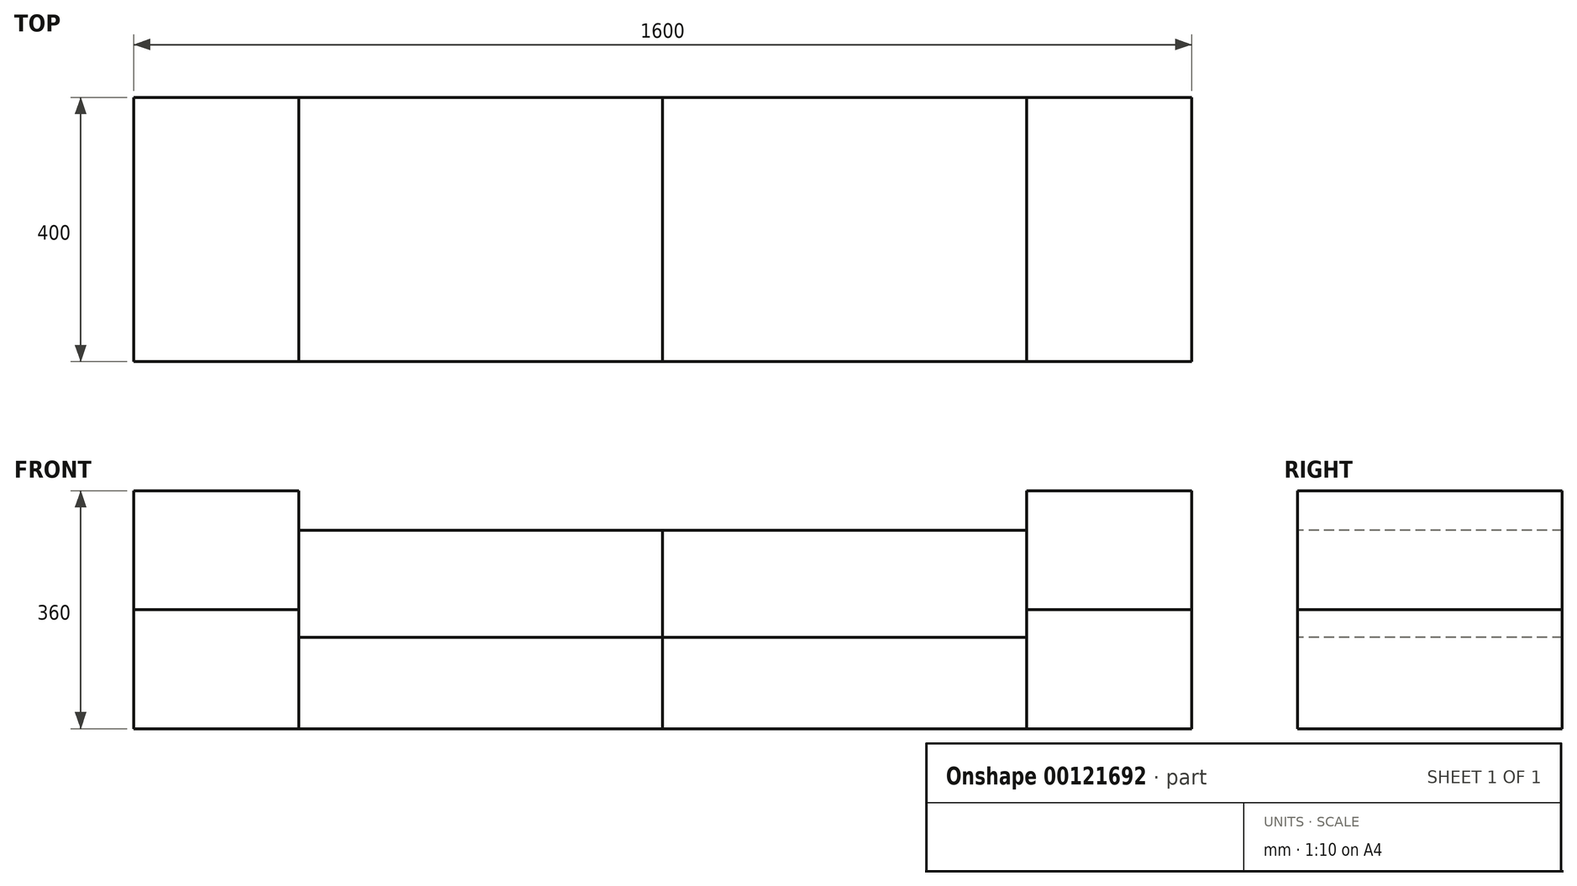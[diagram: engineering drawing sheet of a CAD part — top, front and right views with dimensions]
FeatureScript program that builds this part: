
annotation { "Feature Type Name" : "Feature", "Feature Type Description" : "" }
export const myFeature = defineFeature(function(context is Context, id is Id, definition is map)
    precondition{}
    {
        {
            var Q0;
            Q0=qCreatedBy(makeId("Front.planeOp"),FACE);
            var sketch = newSketch(context, id + "F0", { "sketchPlane" : qUnion([Q0])});
            skLineSegment(sketch, "E0", {"start": v(0, 0) * mm, "end": v(1600, 0) * mm});
            skLineSegment(sketch, "E1", {"start": v(1600, 0) * mm, "end": v(1600, 360) * mm});
            skLineSegment(sketch, "E2", {"start": v(1600, 360) * mm, "end": v(1350, 360) * mm});
            skLineSegment(sketch, "E3", {"start": v(1350, 360) * mm, "end": v(1350, 0) * mm});
            skLineSegment(sketch, "E4", {"start": v(1350, 300) * mm, "end": v(250, 300) * mm});
            skLineSegment(sketch, "E5", {"start": v(250, 0) * mm, "end": v(250, 360) * mm});
            skLineSegment(sketch, "E6", {"start": v(250, 360) * mm, "end": v(0, 360) * mm});
            skLineSegment(sketch, "E7", {"start": v(0, 360) * mm, "end": v(0, 0) * mm});
            skLineSegment(sketch, "E8", {"start": v(250, 137.84) * mm, "end": v(1350, 137.84) * mm});
            skLineSegment(sketch, "E9", {"start": v(800, 300) * mm, "end": v(800, 0) * mm});
            skLineSegment(sketch, "E10", {"start": v(250, 180) * mm, "end": v(0, 180) * mm});
            skLineSegment(sketch, "E11", {"start": v(1350, 180) * mm, "end": v(1600, 180) * mm});
            skSolve(sketch);
        }
        {
            var Q0;
            Q0 = qSketchRegion(id + "F0", true);
            var Q1;
            Q1=sQuery(id+"F0.wireOp",EDGE,"E7");
            var Q2;
            Q2=sQuery(id+"F0.wireOp",EDGE,"E1");
            var Q3;
            Q3=sQuery(id+"F0.wireOp",EDGE,"E0");
            var Q4;
            Q4=sQuery(id+"F0.wireOp",EDGE,"E6");
            var Q5;
            Q5=sQuery(id+"F0.wireOp",EDGE,"E2");
            var Q6;
            Q6=sQuery(id+"F0.wireOp",EDGE,"E4");
            var Q7;
            Q7=sQuery(id+"F0.wireOp",EDGE,"E8");
            extrude(context, id + "F1", {"entities" : qUnion([Q0]), "bodyType" : ToolBodyType.SURFACE, "surfaceEntities" : qUnion([Q1, Q2, Q3, Q4, Q5, Q6, Q7]), "depth" : 400 * mm});
        }
        {
            var Q0;
            Q0 = qSketchRegion(id + "F0", true);
            var Q1;
            Q1=sQuery(id+"F0.wireOp",EDGE,"E5");
            var Q2;
            Q2=sQuery(id+"F0.wireOp",EDGE,"E3");
            var Q3;
            Q3=sQuery(id+"F0.wireOp",EDGE,"E9");
            extrude(context, id + "F2", {"entities" : qUnion([Q0]), "bodyType" : ToolBodyType.SURFACE, "surfaceEntities" : qUnion([Q1, Q2, Q3]), "depth" : 400 * mm});
        }
        {
            var Q0;
            {var subQ3=sQuery(id+"F0.wireOp",EDGE,"E2");Q0=makeQuery(id+"F0.imprint","IMPRINT",FACE,{"disambiguationData":[TD([[makeQuery(id+"F0.imprint","IMPRINT",EDGE,{"derivedFrom":subQ3}),1.0]])]});}
            var Q1;
            {var subQ1=sQuery(id+"F0.wireOp",EDGE,"E6");Q1=makeQuery(id+"F0.imprint","IMPRINT",FACE,{"disambiguationData":[TD([[makeQuery(id+"F0.imprint","IMPRINT",EDGE,{"derivedFrom":subQ1}),1.0]])]});}
            var Q2;
            {var subQ0=sQuery(id+"F0.wireOp",EDGE,"E5");var subQ1=sQuery(id+"F0.wireOp",EDGE,"E0");var subQ2=makeQuery(id+"F0.imprint","INTERSECT",VERTEX,{"derivedFrom":[subQ1,subQ0]});Q2=makeQuery(id+"F0.imprint","IMPRINT",FACE,{"disambiguationData":[TD([[makeQuery(id+"F0.imprint","IMPRINT",EDGE,{"disambiguationData":[TD([[subQ2,-1.0]])],"derivedFrom":subQ1}),1.0]])]});}
            var Q3;
            {var subQ0=sQuery(id+"F0.wireOp",EDGE,"E3");var subQ1=sQuery(id+"F0.wireOp",EDGE,"E0");var subQ2=makeQuery(id+"F0.imprint","INTERSECT",VERTEX,{"derivedFrom":[subQ1,subQ0]});Q3=makeQuery(id+"F0.imprint","IMPRINT",FACE,{"disambiguationData":[TD([[makeQuery(id+"F0.imprint","IMPRINT",EDGE,{"disambiguationData":[TD([[subQ2,1.0]])],"derivedFrom":subQ1}),1.0]])]});}
            var Q4;
            {var subQ6=sQuery(id+"F0.wireOp",EDGE,"E11");Q4=makeQuery(id+"F0.imprint","IMPRINT",FACE,{"disambiguationData":[TD([[makeQuery(id+"F0.imprint","IMPRINT",EDGE,{"derivedFrom":subQ6}),-1.0]])]});}
            var Q5;
            {var subQ1=sQuery(id+"F0.wireOp",EDGE,"E3");var subQ5=sQuery(id+"F0.wireOp",EDGE,"E4");var subQ6=makeQuery(id+"F0.imprint","INTERSECT",VERTEX,{"derivedFrom":[subQ1,subQ5]});Q5=makeQuery(id+"F0.imprint","IMPRINT",FACE,{"disambiguationData":[TD([[makeQuery(id+"F0.imprint","IMPRINT",EDGE,{"disambiguationData":[TD([[subQ6,-1.0]])],"derivedFrom":subQ1}),-1.0]])]});}
            var Q6;
            {var subQ1=sQuery(id+"F0.wireOp",EDGE,"E5");var subQ5=sQuery(id+"F0.wireOp",EDGE,"E4");var subQ6=makeQuery(id+"F0.imprint","INTERSECT",VERTEX,{"derivedFrom":[subQ5,subQ1]});Q6=makeQuery(id+"F0.imprint","IMPRINT",FACE,{"disambiguationData":[TD([[makeQuery(id+"F0.imprint","IMPRINT",EDGE,{"disambiguationData":[TD([[subQ6,1.0]])],"derivedFrom":subQ5}),1.0]])]});}
            var Q7;
            Q7=sQuery(id+"F0.wireOp",EDGE,"E10");
            var Q8;
            Q8=sQuery(id+"F0.wireOp",EDGE,"E11");
            extrude(context, id + "F3", {"entities" : qUnion([Q0, Q1, Q2, Q3, Q4, Q5, Q6]), "bodyType" : ToolBodyType.SURFACE, "surfaceEntities" : qUnion([Q7, Q8]), "depth" : 400 * mm});
        }
    });
